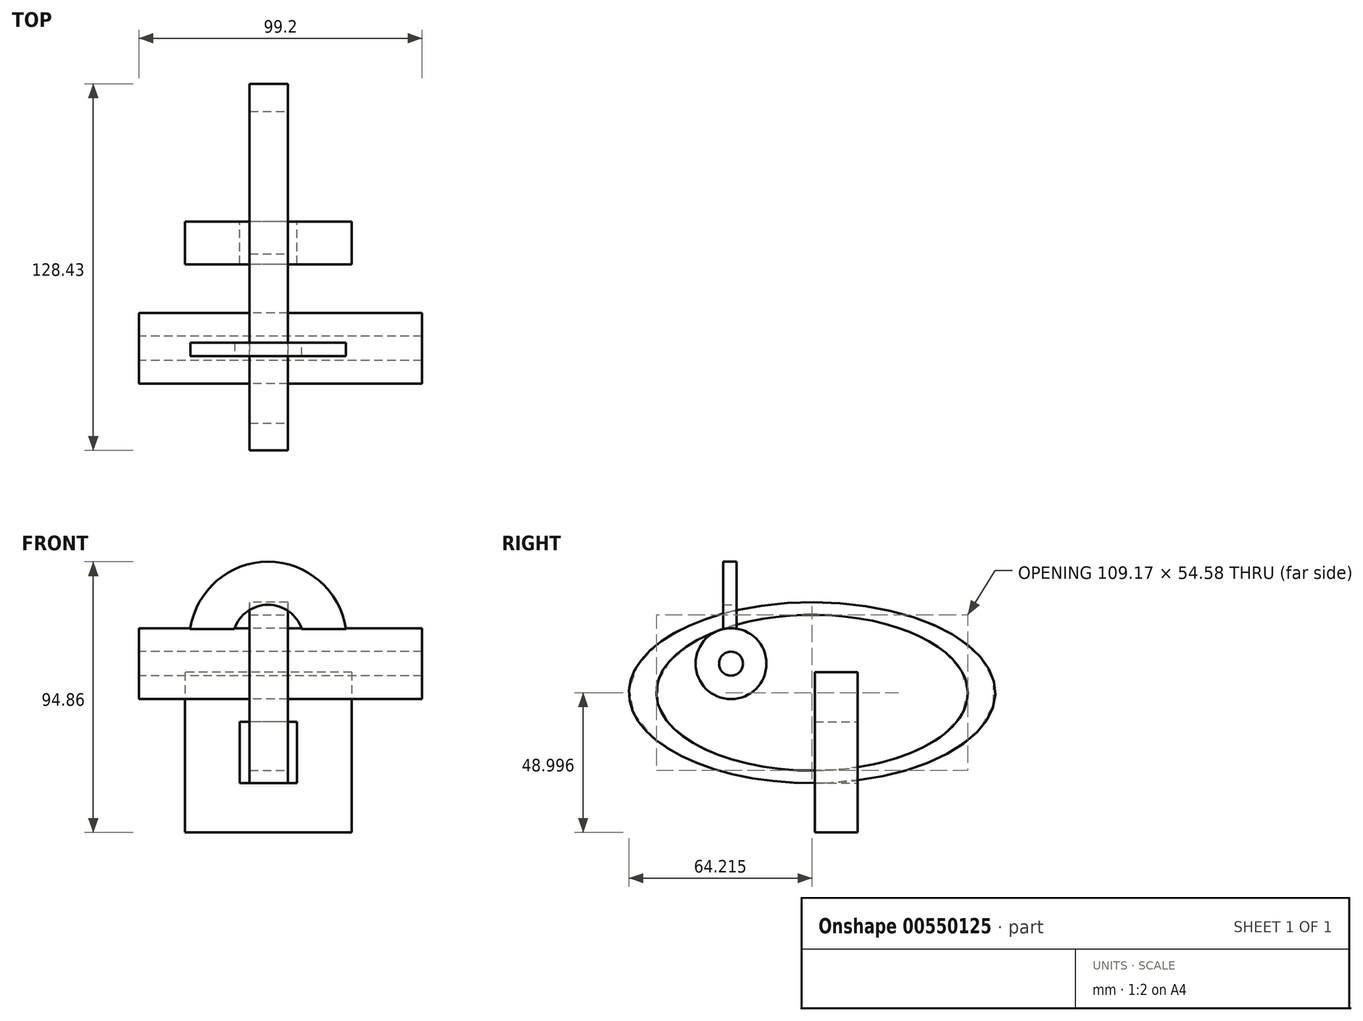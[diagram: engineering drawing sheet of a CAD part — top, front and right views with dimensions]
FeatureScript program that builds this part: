
annotation { "Feature Type Name" : "Feature", "Feature Type Description" : "" }
export const myFeature = defineFeature(function(context is Context, id is Id, definition is map)
    precondition{}
    {
        {
            var Q0;
            Q0=qCreatedBy(makeId("Front.planeOp"),FACE);
            var sketch = newSketch(context, id + "F0", { "sketchPlane" : qUnion([Q0])});
            skLineSegment(sketch, "E0.bottom", {"start": v(0.41, -7.22) * mm, "end": v(-58.06, -7.22) * mm});
            skLineSegment(sketch, "E0.top", {"start": v(0.41, -63.45) * mm, "end": v(-58.06, -63.45) * mm});
            skLineSegment(sketch, "E0.left", {"start": v(0.41, -7.22) * mm, "end": v(0.41, -63.45) * mm});
            skLineSegment(sketch, "E0.right", {"start": v(-58.06, -7.22) * mm, "end": v(-58.06, -63.45) * mm});
            skPoint(sketch, "E0.middle", {"position": v(-28.82, -35.34) * mm});
            skLineSegment(sketch, "E1.bottom", {"start": v(-18.83, -24.6) * mm, "end": v(-38.82, -24.6) * mm});
            skLineSegment(sketch, "E1.top", {"start": v(-18.83, -46.07) * mm, "end": v(-38.82, -46.07) * mm});
            skLineSegment(sketch, "E1.left", {"start": v(-18.83, -24.6) * mm, "end": v(-18.83, -46.07) * mm});
            skLineSegment(sketch, "E1.right", {"start": v(-38.82, -24.6) * mm, "end": v(-38.82, -46.07) * mm});
            skSolve(sketch);
        }
        {
            var Q0;
            Q0 = qSketchRegion(id + "F0", true);
            extrude(context, id + "F1", {"entities" : qUnion([Q0]), "depth" : 15 * mm, "offsetDistance" : 25 * mm});
        }
        {
            var Q0;
            Q0=qCreatedBy(makeId("Right.planeOp"),FACE);
            var sketch = newSketch(context, id + "F2", { "sketchPlane" : qUnion([Q0])});
            skEllipse(sketch, "E2", {"center": v(-15.99, -14.45) * mm, "majorRadius": 54.58 * mm, "minorRadius": 27.3 * mm, "majorAxis": v(1, 0)});
            skEllipse(sketch, "E3", {"center": v(-15.99, -14.45) * mm, "majorRadius": 64.22 * mm, "minorRadius": 31.7 * mm, "majorAxis": v(1, 0)});
            skCircle(sketch, "E4", {"center": v(-44.4, -4.28) * mm, "radius": 12.41 * mm});
            skCircle(sketch, "E5", {"center": v(-44.4, -4.28) * mm, "radius": 4.2 * mm});
            skSolve(sketch);
        }
        {
            var Q0;
            Q0 = qSketchRegion(id + "F2", true);
            extrude(context, id + "F3", {"entities" : qUnion([Q0]), "operationType" : NewBodyOperationType.ADD, "oppositeDirection" : true, "depth" : 35.4 * mm, "offsetDistance" : 25 * mm, "hasSecondDirection" : true, "secondDirectionOppositeDirection" : true, "secondDirectionDepth" : 22 * mm});
        }
        {
            var Q0;
            Q0=makeQuery(id+"F2.imprint","IMPRINT",FACE,{"disambiguationData":[TD([[makeQuery(id+"F2.imprint","IMPRINT",EDGE,{"derivedFrom":sQuery(id+"F2.wireOp",EDGE,"E4")}),1.0]])]});
            extrude(context, id + "F4", {"entities" : qUnion([Q0]), "operationType" : NewBodyOperationType.ADD, "depth" : 25 * mm, "offsetDistance" : 25 * mm, "hasSecondDirection" : true, "secondDirectionOppositeDirection" : true, "secondDirectionDepth" : 74.2 * mm});
        }
        {
            var Q0;
            Q0=qCreatedBy(makeId("Front.planeOp"),FACE);
            var sketch = newSketch(context, id + "F5", { "sketchPlane" : qUnion([Q0])});
            skArc(sketch, "E6", {"start": v(-17.05, 7.72) * mm, "mid": v(-28.92, 16.33) * mm, "end": v(-40.8, 7.74) * mm});
            skArc(sketch, "E7", {"start": v(-1.65, 7.83) * mm, "mid": v(-29.04, 31.4) * mm, "end": v(-56.24, 7.6) * mm});
            skLineSegment(sketch, "E8", {"start": v(-1.65, 7.83) * mm, "end": v(-17.05, 7.72) * mm});
            skLineSegment(sketch, "E9", {"start": v(-40.8, 7.74) * mm, "end": v(-56.24, 7.6) * mm});
            skSolve(sketch);
        }
        {
            var Q0;
            Q0 = qSketchRegion(id + "F5", true);
            extrude(context, id + "F6", {"entities" : qUnion([Q0]), "operationType" : NewBodyOperationType.ADD, "depth" : 47.1 * mm, "offsetDistance" : 25 * mm, "hasSecondDirection" : true, "secondDirectionOppositeDirection" : false, "secondDirectionDepth" : 42.4 * mm});
        }
    });
